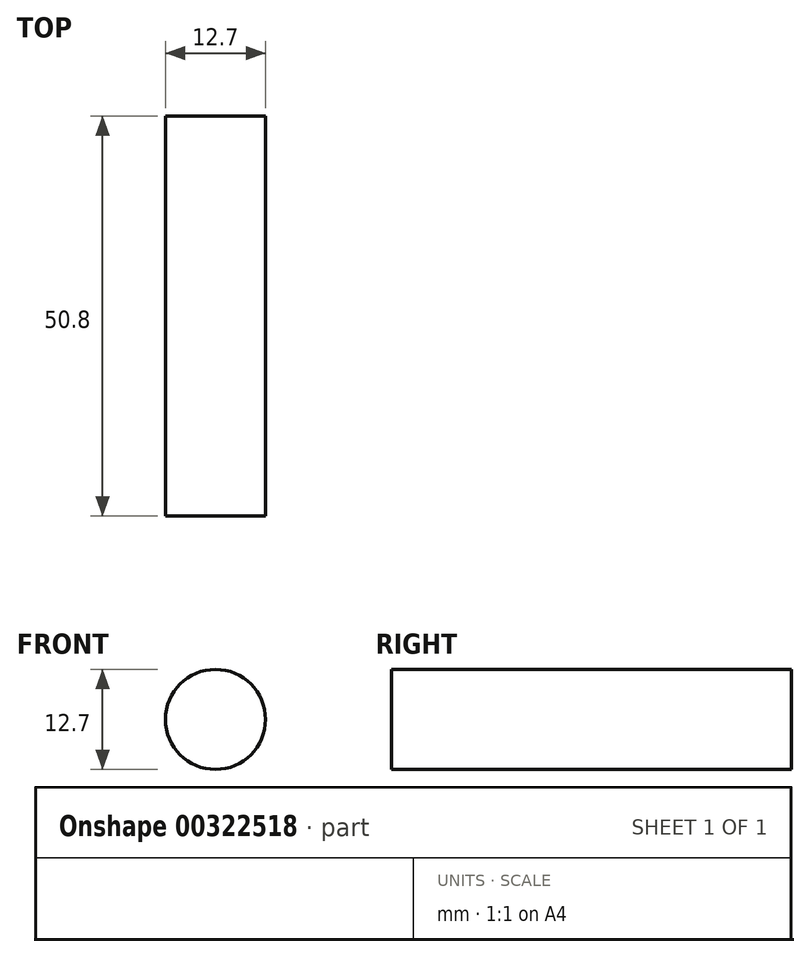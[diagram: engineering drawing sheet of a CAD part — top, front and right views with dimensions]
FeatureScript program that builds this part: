
annotation { "Feature Type Name" : "Feature", "Feature Type Description" : "" }
export const myFeature = defineFeature(function(context is Context, id is Id, definition is map)
    precondition{}
    {
        {
            var Q0;
            Q0=qCreatedBy(makeId("Front.planeOp"),FACE);
            var sketch = newSketch(context, id + "F0", { "sketchPlane" : qUnion([Q0])});
            skLineSegment(sketch, "E0.bottom", {"start": v(25.4, -25.4) * mm, "end": v(-25.4, -25.4) * mm});
            skPoint(sketch, "E0.middle", {"position": v(0, 0) * mm});
            skLineSegment(sketch, "E1", {"start": v(-25.4, 25.4) * mm, "end": v(0, 69.4) * mm});
            skLineSegment(sketch, "E2", {"start": v(0, 69.4) * mm, "end": v(25.4, 25.4) * mm});
            skLineSegment(sketch, "E3.0", {"start": v(25.03, -25.4) * mm, "end": v(25.03, 25.4) * mm});
            skLineSegment(sketch, "E4", {"start": v(-25.4, 25.4) * mm, "end": v(-25.4, -25.4) * mm});
            skCircle(sketch, "E5", {"center": v(-10.58, -7.6) * mm, "radius": 6.35 * mm});
            skSolve(sketch);
        }
        {
            var Q0;
            Q0 = qSketchRegion(id + "F0", true);
            extrude(context, id + "F1", {"entities" : qUnion([Q0]), "depth" : 50.8 * mm});
        }
    });
